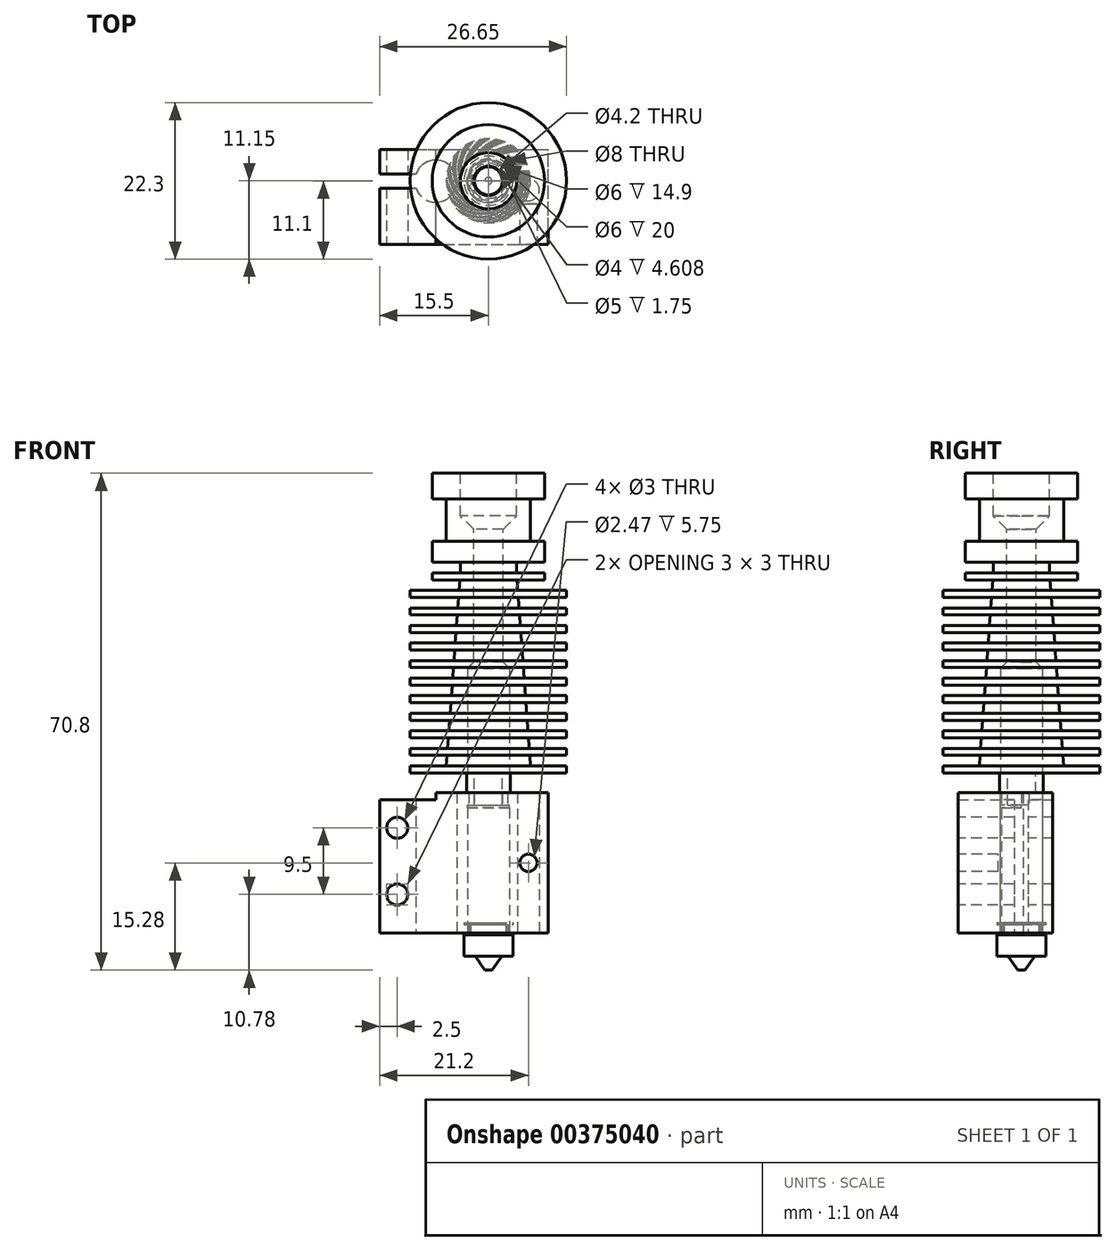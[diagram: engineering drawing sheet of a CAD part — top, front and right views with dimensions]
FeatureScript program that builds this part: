
annotation { "Feature Type Name" : "Feature", "Feature Type Description" : "" }
export const myFeature = defineFeature(function(context is Context, id is Id, definition is map)
    precondition{}
    {
        {
            var Q0;
            Q0=qCreatedBy(makeId("Top.planeOp"),FACE);
            var sketch = newSketch(context, id + "F0", { "sketchPlane" : qUnion([Q0])});
            skCircle(sketch, "E0", {"center": v(0, 0) * mm, "radius": 8 * mm});
            skSolve(sketch);
        }
        {
            var Q0;
            Q0=makeQuery(id+"F0.imprint","IMPRINT",FACE,{"disambiguationData":[TD([[makeQuery(id+"F0.imprint","IMPRINT",EDGE,{"derivedFrom":sQuery(id+"F0.wireOp",EDGE,"E0")}),1.0]])]});
            var Q1;
            Q1=sQuery(id+"F0.wireOp",EDGE,"E0");
            extrude(context, id + "F1", {"entities" : qUnion([Q0]), "surfaceEntities" : qUnion([Q1]), "oppositeDirection" : true, "depth" : 3.7 * mm});
        }
        {
            var Q0;
            Q0=makeQuery(id+"F1.opExtrude","CAP_FACE",FACE,{"disambiguationData":[OSD([sQuery(id+"F0.wireOp",EDGE,"E0")])],"isStart":false});
            var sketch = newSketch(context, id + "F2", { "sketchPlane" : qUnion([Q0])});
            skCircle(sketch, "E1", {"center": v(0, 0) * mm, "radius": 6 * mm});
            skSolve(sketch);
        }
        {
            var Q0;
            Q0=makeQuery(id+"F2.imprint","IMPRINT",FACE,{"disambiguationData":[TD([[makeQuery(id+"F2.imprint","IMPRINT",EDGE,{"derivedFrom":sQuery(id+"F2.wireOp",EDGE,"E1")}),1.0]])]});
            var Q1;
            Q1=sQuery(id+"F2.wireOp",EDGE,"E1");
            extrude(context, id + "F3", {"entities" : qUnion([Q0]), "operationType" : NewBodyOperationType.ADD, "surfaceEntities" : qUnion([Q1]), "depth" : 6 * mm});
        }
        {
            var Q0;
            Q0=makeQuery(id+"F3.opExtrude","CAP_FACE",FACE,{"disambiguationData":[OSD([sQuery(id+"F2.wireOp",EDGE,"E1")])],"isStart":false});
            var sketch = newSketch(context, id + "F4", { "sketchPlane" : qUnion([Q0])});
            skCircle(sketch, "E2", {"center": v(0, 0) * mm, "radius": 8 * mm});
            skSolve(sketch);
        }
        {
            var Q0;
            Q0=qSketchRegion(id+"F4",true);
            extrude(context, id + "F5", {"entities" : qUnion([Q0]), "operationType" : NewBodyOperationType.ADD, "depth" : 3 * mm});
        }
        {
            var Q0;
            Q0=qCreatedBy(makeId("Front.planeOp"),FACE);
            var sketch = newSketch(context, id + "F6", { "sketchPlane" : qUnion([Q0])});
            skLineSegment(sketch, "E3", {"start": v(0, 0) * mm, "end": v(0, -12.7) * mm});
            skLineSegment(sketch, "E4.bottom", {"start": v(0, -12.7) * mm, "end": v(4, -12.7) * mm});
            skLineSegment(sketch, "E4.top", {"start": v(0, -14.2) * mm, "end": v(4, -14.2) * mm});
            skLineSegment(sketch, "E4.left", {"start": v(0, -12.7) * mm, "end": v(0, -14.2) * mm});
            skLineSegment(sketch, "E4.right", {"start": v(4, -12.7) * mm, "end": v(4, -14.2) * mm});
            skLineSegment(sketch, "E5.bottom", {"start": v(0, -14.2) * mm, "end": v(8, -14.2) * mm});
            skLineSegment(sketch, "E5.top", {"start": v(0, -15.2) * mm, "end": v(8, -15.2) * mm});
            skLineSegment(sketch, "E5.left", {"start": v(0, -14.2) * mm, "end": v(0, -15.2) * mm});
            skLineSegment(sketch, "E5.right", {"start": v(8, -14.2) * mm, "end": v(8, -15.2) * mm});
            skLineSegment(sketch, "E6", {"start": v(0, -15.2) * mm, "end": v(0, -16.7) * mm});
            skLineSegment(sketch, "E7.bottom", {"start": v(0, -16.7) * mm, "end": v(11.15, -16.7) * mm});
            skLineSegment(sketch, "E7.top", {"start": v(0, -17.7) * mm, "end": v(11.15, -17.7) * mm});
            skLineSegment(sketch, "E7.left", {"start": v(0, -16.7) * mm, "end": v(0, -17.7) * mm});
            skLineSegment(sketch, "E7.right", {"start": v(11.15, -16.7) * mm, "end": v(11.15, -17.7) * mm});
            skLineSegment(sketch, "E8.1.0.0", {"start": v(0, -20.2) * mm, "end": v(11.15, -20.2) * mm});
            skLineSegment(sketch, "E8.1.0.1", {"start": v(0, -19.2) * mm, "end": v(11.15, -19.2) * mm});
            skLineSegment(sketch, "E8.1.0.2", {"start": v(0, -19.2) * mm, "end": v(0, -20.2) * mm});
            skLineSegment(sketch, "E8.1.0.3", {"start": v(11.15, -19.2) * mm, "end": v(11.15, -20.2) * mm});
            skLineSegment(sketch, "E8.2.0.0", {"start": v(0, -22.7) * mm, "end": v(11.15, -22.7) * mm});
            skLineSegment(sketch, "E8.2.0.1", {"start": v(0, -21.7) * mm, "end": v(11.15, -21.7) * mm});
            skLineSegment(sketch, "E8.2.0.2", {"start": v(0, -21.7) * mm, "end": v(0, -22.7) * mm});
            skLineSegment(sketch, "E8.2.0.3", {"start": v(11.15, -21.7) * mm, "end": v(11.15, -22.7) * mm});
            skLineSegment(sketch, "E8.3.0.0", {"start": v(0, -25.2) * mm, "end": v(11.15, -25.2) * mm});
            skLineSegment(sketch, "E8.3.0.1", {"start": v(0, -24.2) * mm, "end": v(11.15, -24.2) * mm});
            skLineSegment(sketch, "E8.3.0.2", {"start": v(0, -24.2) * mm, "end": v(0, -25.2) * mm});
            skLineSegment(sketch, "E8.3.0.3", {"start": v(11.15, -24.2) * mm, "end": v(11.15, -25.2) * mm});
            skLineSegment(sketch, "E8.4.0.0", {"start": v(0, -27.7) * mm, "end": v(11.15, -27.7) * mm});
            skLineSegment(sketch, "E8.4.0.1", {"start": v(0, -26.7) * mm, "end": v(11.15, -26.7) * mm});
            skLineSegment(sketch, "E8.4.0.2", {"start": v(0, -26.7) * mm, "end": v(0, -27.7) * mm});
            skLineSegment(sketch, "E8.4.0.3", {"start": v(11.15, -26.7) * mm, "end": v(11.15, -27.7) * mm});
            skLineSegment(sketch, "E8.5.0.0", {"start": v(0, -30.2) * mm, "end": v(11.15, -30.2) * mm});
            skLineSegment(sketch, "E8.5.0.1", {"start": v(0, -29.2) * mm, "end": v(11.15, -29.2) * mm});
            skLineSegment(sketch, "E8.5.0.2", {"start": v(0, -29.2) * mm, "end": v(0, -30.2) * mm});
            skLineSegment(sketch, "E8.5.0.3", {"start": v(11.15, -29.2) * mm, "end": v(11.15, -30.2) * mm});
            skLineSegment(sketch, "E8.6.0.0", {"start": v(0, -32.7) * mm, "end": v(11.15, -32.7) * mm});
            skLineSegment(sketch, "E8.6.0.1", {"start": v(0, -31.7) * mm, "end": v(11.15, -31.7) * mm});
            skLineSegment(sketch, "E8.6.0.2", {"start": v(0, -31.7) * mm, "end": v(0, -32.7) * mm});
            skLineSegment(sketch, "E8.6.0.3", {"start": v(11.15, -31.7) * mm, "end": v(11.15, -32.7) * mm});
            skLineSegment(sketch, "E8.7.0.0", {"start": v(0, -35.2) * mm, "end": v(11.15, -35.2) * mm});
            skLineSegment(sketch, "E8.7.0.1", {"start": v(0, -34.2) * mm, "end": v(11.15, -34.2) * mm});
            skLineSegment(sketch, "E8.7.0.2", {"start": v(0, -34.2) * mm, "end": v(0, -35.2) * mm});
            skLineSegment(sketch, "E8.7.0.3", {"start": v(11.15, -34.2) * mm, "end": v(11.15, -35.2) * mm});
            skLineSegment(sketch, "E8.8.0.0", {"start": v(0, -37.7) * mm, "end": v(11.15, -37.7) * mm});
            skLineSegment(sketch, "E8.8.0.1", {"start": v(0, -36.7) * mm, "end": v(11.15, -36.7) * mm});
            skLineSegment(sketch, "E8.8.0.2", {"start": v(0, -36.7) * mm, "end": v(0, -37.7) * mm});
            skLineSegment(sketch, "E8.8.0.3", {"start": v(11.15, -36.7) * mm, "end": v(11.15, -37.7) * mm});
            skLineSegment(sketch, "E8.9.0.0", {"start": v(0, -40.2) * mm, "end": v(11.15, -40.2) * mm});
            skLineSegment(sketch, "E8.9.0.1", {"start": v(0, -39.2) * mm, "end": v(11.15, -39.2) * mm});
            skLineSegment(sketch, "E8.9.0.2", {"start": v(0, -39.2) * mm, "end": v(0, -40.2) * mm});
            skLineSegment(sketch, "E8.9.0.3", {"start": v(11.15, -39.2) * mm, "end": v(11.15, -40.2) * mm});
            skLineSegment(sketch, "E8.10.0.0", {"start": v(0, -42.7) * mm, "end": v(11.15, -42.7) * mm});
            skLineSegment(sketch, "E8.10.0.1", {"start": v(0, -41.7) * mm, "end": v(11.15, -41.7) * mm});
            skLineSegment(sketch, "E8.10.0.2", {"start": v(0, -41.7) * mm, "end": v(0, -42.7) * mm});
            skLineSegment(sketch, "E8.10.0.3", {"start": v(11.15, -41.7) * mm, "end": v(11.15, -42.7) * mm});
            skLineSegment(sketch, "E8.direction1", {"start": v(0, -17.7) * mm, "end": v(0, -20.2) * mm, "construction": true});
            skLineSegment(sketch, "E9", {"start": v(0, -41.7) * mm, "end": v(6, -41.7) * mm});
            skLineSegment(sketch, "E10", {"start": v(4.07, -15.2) * mm, "end": v(4.18, -16.7) * mm});
            skLineSegment(sketch, "E11.trimOffspring", {"start": v(4.25, -17.7) * mm, "end": v(4.36, -19.2) * mm});
            skLineSegment(sketch, "E12.trimOffspring", {"start": v(4.44, -20.2) * mm, "end": v(4.55, -21.7) * mm});
            skLineSegment(sketch, "E13.trimOffspring", {"start": v(4.62, -22.7) * mm, "end": v(4.73, -24.2) * mm});
            skLineSegment(sketch, "E14.trimOffspring", {"start": v(4.8, -25.2) * mm, "end": v(4.9, -26.7) * mm});
            skLineSegment(sketch, "E15.trimOffspring", {"start": v(4.98, -27.7) * mm, "end": v(5.1, -29.2) * mm});
            skLineSegment(sketch, "E16.trimOffspring", {"start": v(5.16, -30.2) * mm, "end": v(5.27, -31.7) * mm});
            skLineSegment(sketch, "E17.trimOffspring", {"start": v(5.35, -32.7) * mm, "end": v(5.45, -34.2) * mm});
            skLineSegment(sketch, "E18.trimOffspring", {"start": v(5.53, -35.2) * mm, "end": v(5.64, -36.7) * mm});
            skLineSegment(sketch, "E19.trimOffspring", {"start": v(5.7, -37.7) * mm, "end": v(5.82, -39.2) * mm});
            skLineSegment(sketch, "E20.trimOffspring", {"start": v(5.9, -40.2) * mm, "end": v(6, -41.7) * mm});
            skLineSegment(sketch, "E21", {"start": v(0, -17.7) * mm, "end": v(0, -19.2) * mm});
            skLineSegment(sketch, "E22", {"start": v(0, -20.2) * mm, "end": v(0, -21.7) * mm});
            skLineSegment(sketch, "E23", {"start": v(0, -22.7) * mm, "end": v(0, -24.2) * mm});
            skLineSegment(sketch, "E24", {"start": v(0, -25.2) * mm, "end": v(0, -26.7) * mm});
            skLineSegment(sketch, "E25", {"start": v(0, -27.7) * mm, "end": v(0, -29.2) * mm});
            skLineSegment(sketch, "E26", {"start": v(0, -30.2) * mm, "end": v(0, -31.7) * mm});
            skLineSegment(sketch, "E27", {"start": v(0, -32.7) * mm, "end": v(0, -34.2) * mm});
            skLineSegment(sketch, "E28", {"start": v(0, -35.2) * mm, "end": v(0, -36.7) * mm});
            skLineSegment(sketch, "E29", {"start": v(0, -37.7) * mm, "end": v(0, -39.2) * mm});
            skLineSegment(sketch, "E30", {"start": v(0, -40.2) * mm, "end": v(0, -41.7) * mm});
            skLineSegment(sketch, "E31.right", {"start": v(3, -42.7) * mm, "end": v(3, -45.2) * mm});
            skLineSegment(sketch, "E32", {"start": v(3, -45.2) * mm, "end": v(2, -45.2) * mm});
            skLineSegment(sketch, "E33", {"start": v(2, -45.2) * mm, "end": v(2, -42.7) * mm});
            skLineSegment(sketch, "E34.bottom", {"start": v(2, -45.2) * mm, "end": v(3, -45.2) * mm});
            skLineSegment(sketch, "E34.top", {"start": v(2, -47.3) * mm, "end": v(3, -47.3) * mm});
            skLineSegment(sketch, "E34.left", {"start": v(2, -45.2) * mm, "end": v(2, -47.3) * mm});
            skLineSegment(sketch, "E34.right", {"start": v(3, -45.2) * mm, "end": v(3, -47.3) * mm});
            skLineSegment(sketch, "E35.bottom", {"start": v(3, -47.3) * mm, "end": v(3.75, -47.3) * mm});
            skLineSegment(sketch, "E35.top", {"start": v(3, -46.56) * mm, "end": v(3.75, -46.56) * mm});
            skLineSegment(sketch, "E35.left", {"start": v(3, -47.3) * mm, "end": v(3, -46.56) * mm});
            skLineSegment(sketch, "E35.right", {"start": v(3.75, -47.3) * mm, "end": v(3.75, -46.56) * mm});
            skLineSegment(sketch, "E36.bottom", {"start": v(2, -42.7) * mm, "end": v(3, -42.7) * mm});
            skLineSegment(sketch, "E36.top", {"start": v(2, -41.7) * mm, "end": v(3, -41.7) * mm});
            skLineSegment(sketch, "E36.left", {"start": v(2, -42.7) * mm, "end": v(2, -41.7) * mm});
            skLineSegment(sketch, "E36.right", {"start": v(3, -42.7) * mm, "end": v(3, -41.7) * mm});
            skSolve(sketch);
        }
        {
            var Q0;
            Q0=qSketchRegion(id+"F6",true);
            var Q1;
            {var subQ0=sQuery(id+"F6.wireOp",EDGE,"E31.right");Q1=makeQuery(id+"F6.imprint","IMPRINT",FACE,{"disambiguationData":[TD([[makeQuery(id+"F6.imprint","IMPRINT",EDGE,{"derivedFrom":subQ0}),-1.0]])]});}
            var Q2;
            Q2=makeQuery(id+"F6.imprint","IMPRINT",FACE,{"disambiguationData":[TD([[makeQuery(id+"F6.imprint","IMPRINT",EDGE,{"derivedFrom":sQuery(id+"F6.wireOp",EDGE,"E34.bottom")}),-1.0]])]});
            var Q3;
            Q3=makeQuery(id+"F6.imprint","IMPRINT",FACE,{"disambiguationData":[TD([[makeQuery(id+"F6.imprint","IMPRINT",EDGE,{"derivedFrom":sQuery(id+"F6.wireOp",EDGE,"E36.bottom")}),1.0]])]});
            var Q4;
            Q4=makeQuery(id+"F6.imprint","IMPRINT",FACE,{"disambiguationData":[TD([[makeQuery(id+"F6.imprint","IMPRINT",EDGE,{"derivedFrom":sQuery(id+"F6.wireOp",EDGE,"E31.right")}),-1.0]])]});
            var Q5;
            Q5=makeQuery(id+"F6.imprint","IMPRINT",FACE,{"disambiguationData":[TD([[makeQuery(id+"F6.imprint","IMPRINT",EDGE,{"derivedFrom":sQuery(id+"F6.wireOp",EDGE,"E34.bottom")}),-1.0]])]});
            var Q6;
            Q6=sQuery(id+"F6.wireOp",EDGE,"E3");
            revolve(context, id + "F7", {"operationType" : NewBodyOperationType.ADD, "entities" : qUnion([Q0, Q1, Q2, Q3, Q4, Q5]), "axis" : qUnion([Q6]), "revolveType" : RevolveType.FULL});
        }
        {
            var Q0;
            Q0=makeQuery(id+"F1.opExtrude","CAP_FACE",FACE,{"disambiguationData":[OSD([sQuery(id+"F0.wireOp",EDGE,"E0")])],"isStart":true});
            var sketch = newSketch(context, id + "F8", { "sketchPlane" : qUnion([Q0])});
            skCircle(sketch, "E37", {"center": v(0, 0) * mm, "radius": 2.1 * mm});
            skSolve(sketch);
        }
        {
            var Q0;
            Q0=qSketchRegion(id+"F8",true);
            extrude(context, id + "F9", {"entities" : qUnion([Q0]), "operationType" : NewBodyOperationType.REMOVE, "oppositeDirection" : true, "depth" : 42.7 * mm});
        }
        {
            var Q0;
            Q0=makeQuery(id+"F1.opExtrude","CAP_FACE",FACE,{"disambiguationData":[OSD([sQuery(id+"F0.wireOp",EDGE,"E0")])],"isStart":true});
            var sketch = newSketch(context, id + "F10", { "sketchPlane" : qUnion([Q0])});
            skCircle(sketch, "E38", {"center": v(0, 0) * mm, "radius": 4 * mm});
            skSolve(sketch);
        }
        {
            var Q0;
            Q0=qSketchRegion(id+"F10",true);
            extrude(context, id + "F11", {"entities" : qUnion([Q0]), "operationType" : NewBodyOperationType.REMOVE, "oppositeDirection" : true, "depth" : 6 * mm});
        }
        {
            var Q0;
            Q0=makeQuery(id+"F11.boolean.opBoolean","INTERSECT",EDGE,{"derivedFrom":[makeQuery(id+"F9.boolean.opBoolean","COPY",FACE,{"derivedFrom":makeQuery(id+"F9.opExtrude","SWEPT_FACE",FACE,{"disambiguationData":[OSD([sQuery(id+"F8.wireOp",EDGE,"E37")])]})}),makeQuery(id+"F11.opExtrude","CAP_FACE",FACE,{"disambiguationData":[OSD([sQuery(id+"F10.wireOp",EDGE,"E38")])],"isStart":false})]});
            chamfer(context, id + "F12", {"entities" : qUnion([Q0]), "width" : 2 * mm, "tangentPropagation" : true});
        }
        {
            var Q0;
            Q0=makeQuery(id+"F7.opRevolve","SWEPT_FACE",FACE,{"disambiguationData":[OSD([sQuery(id+"F6.wireOp",EDGE,"E8.10.0.0")])]});
            var sketch = newSketch(context, id + "F13", { "sketchPlane" : qUnion([Q0])});
            skCircle(sketch, "E39", {"center": v(0, 0) * mm, "radius": 3 * mm});
            skSolve(sketch);
        }
        {
            var Q0;
            Q0=qSketchRegion(id+"F13",true);
            extrude(context, id + "F14", {"entities" : qUnion([Q0]), "operationType" : NewBodyOperationType.REMOVE, "oppositeDirection" : true, "depth" : 14.8 * mm});
        }
        {
            var Q0;
            Q0=makeQuery(id+"F14.boolean.opBoolean","INTERSECT",EDGE,{"derivedFrom":[makeQuery(id+"F9.boolean.opBoolean","COPY",FACE,{"derivedFrom":makeQuery(id+"F9.opExtrude","SWEPT_FACE",FACE,{"disambiguationData":[OSD([sQuery(id+"F8.wireOp",EDGE,"E37")])]})}),makeQuery(id+"F14.opExtrude","CAP_FACE",FACE,{"disambiguationData":[OSD([sQuery(id+"F13.wireOp",EDGE,"E39")])],"isStart":false})]});
            chamfer(context, id + "F15", {"entities" : qUnion([Q0]), "width" : 1 * mm, "tangentPropagation" : true});
        }
        {
            var Q0;
            Q0=qCreatedBy(makeId("Front.planeOp"),FACE);
            var sketch = newSketch(context, id + "F16", { "sketchPlane" : qUnion([Q0])});
            skLineSegment(sketch, "E40.bottom", {"start": v(-7.5, -45.52) * mm, "end": v(8.5, -45.52) * mm});
            skLineSegment(sketch, "E40.top", {"start": v(-15.5, -65.52) * mm, "end": v(8.5, -65.52) * mm});
            skLineSegment(sketch, "E40.right", {"start": v(8.5, -45.52) * mm, "end": v(8.5, -65.52) * mm});
            skLineSegment(sketch, "E41", {"start": v(-15.5, -46.52) * mm, "end": v(-15.5, -65.52) * mm});
            skLineSegment(sketch, "E42", {"start": v(-7.5, -45.52) * mm, "end": v(-7.5, -46.52) * mm});
            skLineSegment(sketch, "E43", {"start": v(-15.5, -46.52) * mm, "end": v(-7.5, -46.52) * mm});
            skSolve(sketch);
        }
        {
            var Q0;
            Q0=makeQuery(id+"F16.imprint","IMPRINT",FACE,{"disambiguationData":[TD([[makeQuery(id+"F16.imprint","IMPRINT",EDGE,{"derivedFrom":sQuery(id+"F16.wireOp",EDGE,"E40.bottom")}),-1.0]])]});
            var Q1;
            Q1=makeQuery(id+"F16.imprint","IMPRINT",FACE,{"disambiguationData":[TD([[makeQuery(id+"F16.imprint","IMPRINT",EDGE,{"derivedFrom":sQuery(id+"F16.wireOp",EDGE,"hSTLO5rz-Z077-ZaO5-nEVS-phWlFBx8dYmu")}),1.0]])]});
            var Q2;
            Q2=makeQuery(id+"F16.imprint","IMPRINT",FACE,{"disambiguationData":[TD([[makeQuery(id+"F16.imprint","IMPRINT",EDGE,{"derivedFrom":sQuery(id+"F16.wireOp",EDGE,"1ucrc5hz-Jwvr-DOmE-K7qY-mdj6J8iSEPF0")}),1.0]])]});
            extrude(context, id + "F17", {"entities" : qUnion([Q0, Q1, Q2]), "endBound" : BoundingType.SYMMETRIC, "depth" : 13.5 * mm});
        }
        {
            var Q0;
            Q0=makeQuery(id+"F17.opExtrude","SWEPT_FACE",FACE,{"disambiguationData":[OSD([sQuery(id+"F16.wireOp",EDGE,"E40.top")])]});
            var sketch = newSketch(context, id + "F18", { "sketchPlane" : qUnion([Q0])});
            skCircle(sketch, "E44", {"center": v(0, -2.25) * mm, "radius": 3 * mm});
            skCircle(sketch, "E45", {"center": v(5.7, -1) * mm, "radius": 1.55 * mm});
            skArc(sketch, "E46", {"start": v(-10.33, -3.25) * mm, "mid": v(-4.5, -2.25) * mm, "end": v(-10.33, -1.25) * mm});
            skLineSegment(sketch, "E47.bottom", {"start": v(-15.5, -1.25) * mm, "end": v(-10.33, -1.25) * mm});
            skLineSegment(sketch, "E47.top", {"start": v(-15.5, -3.25) * mm, "end": v(-10.33, -3.25) * mm});
            skLineSegment(sketch, "E47.left", {"start": v(-15.5, -1.25) * mm, "end": v(-15.5, -3.25) * mm});
            skSolve(sketch);
        }
        {
            var Q0;
            Q0=qSketchRegion(id+"F18",true);
            extrude(context, id + "F19", {"entities" : qUnion([Q0]), "operationType" : NewBodyOperationType.REMOVE, "oppositeDirection" : true, "depth" : 20 * mm});
        }
        {
            var Q0;
            Q0=makeQuery(id+"F17.opExtrude","SWEPT_BODY",BODY,{"disambiguationData":[OSD([sQuery(id+"F16.wireOp",EDGE,"E40.bottom"),sQuery(id+"F16.wireOp",EDGE,"E40.top"),sQuery(id+"F16.wireOp",EDGE,"E40.right"),sQuery(id+"F16.wireOp",EDGE,"E41"),sQuery(id+"F16.wireOp",EDGE,"E42"),sQuery(id+"F16.wireOp",EDGE,"E43")])]});
            var Q1;
            Q1=qCreatedBy(makeId("Origin.pointOp"),VERTEX);
            var Q2;
            Q2=makeQuery(id+"F19.boolean.opBoolean","COPY",EDGE,{"derivedFrom":makeQuery(id+"F19.opExtrude","CAP_EDGE",EDGE,{"disambiguationData":[OSD([sQuery(id+"F18.wireOp",EDGE,"E44")])],"isStart":true})});
            var Q3;
            Q3=qCreatedBy(makeId("Front.planeOp"),FACE);
            transform(context, id + "F20", {"entities" : qUnion([Q0]), "transformType" : TransformType.TRANSLATION_DISTANCE, "transformDirection" : qUnion([Q3]), "distance" : 2.3 * mm, "makeCopy" : false});
        }
        {
            var Q0;
            Q0=qCreatedBy(makeId("Front.planeOp"),FACE);
            var sketch = newSketch(context, id + "F21", { "sketchPlane" : qUnion([Q0])});
            skLineSegment(sketch, "E48.bottom", {"start": v(0, -65.8) * mm, "end": v(3.5, -65.8) * mm});
            skLineSegment(sketch, "E48.right", {"start": v(3.5, -65.8) * mm, "end": v(3.5, -68.8) * mm});
            skLineSegment(sketch, "E49.top", {"start": v(0, -70.8) * mm, "end": v(0.5, -70.8) * mm});
            skLineSegment(sketch, "E50", {"start": v(0.5, -70.8) * mm, "end": v(1.9, -68.8) * mm});
            skLineSegment(sketch, "E51.trimOffspring", {"start": v(1.9, -68.8) * mm, "end": v(3.5, -68.8) * mm});
            skLineSegment(sketch, "E52", {"start": v(0, -70.8) * mm, "end": v(0, -65.8) * mm});
            skLineSegment(sketch, "E53", {"start": v(0, -65.8) * mm, "end": v(2.5, -65.8) * mm});
            skLineSegment(sketch, "E54", {"start": v(2.5, -65.8) * mm, "end": v(2.5, -64.3) * mm});
            skLineSegment(sketch, "E55", {"start": v(2.5, -64.3) * mm, "end": v(2.75, -64.3) * mm});
            skLineSegment(sketch, "E56", {"start": v(2.75, -64.3) * mm, "end": v(2.75, -65.8) * mm});
            skLineSegment(sketch, "E57.bottom", {"start": v(2.5, -64.3) * mm, "end": v(3.5, -64.3) * mm});
            skLineSegment(sketch, "E57.top", {"start": v(2.5, -64.05) * mm, "end": v(3.5, -64.05) * mm});
            skLineSegment(sketch, "E57.left", {"start": v(2.5, -64.3) * mm, "end": v(2.5, -64.05) * mm});
            skLineSegment(sketch, "E57.right", {"start": v(3.5, -64.3) * mm, "end": v(3.5, -64.05) * mm});
            skSolve(sketch);
        }
        {
            var Q0;
            Q0=qSketchRegion(id+"F21",true);
            var Q1;
            Q1=sQuery(id+"F21.wireOp",EDGE,"E52");
            revolve(context, id + "F22", {"entities" : qUnion([Q0]), "axis" : qUnion([Q1]), "revolveType" : RevolveType.FULL});
        }
        {
            var Q0;
            Q0=makeQuery(id+"F17.opExtrude","CAP_FACE",FACE,{"disambiguationData":[OSD([sQuery(id+"F16.wireOp",EDGE,"E40.bottom"),sQuery(id+"F16.wireOp",EDGE,"E40.top"),sQuery(id+"F16.wireOp",EDGE,"E40.left"),sQuery(id+"F16.wireOp",EDGE,"E40.right"),sQuery(id+"F16.wireOp",EDGE,"UV7SLQof-a04S-M22U-fSmA-h1v0EtluGPG8"),sQuery(id+"F16.wireOp",EDGE,"g7xF2yxM-ANDZ-qpWR-qvBO-6FQJMMhnbeDq.top"),sQuery(id+"F16.wireOp",EDGE,"L5R9zHDy-imt3-tSqA-0CQm-Dj3PFv1zczeX.top"),sQuery(id+"F16.wireOp",EDGE,"56c6f5e6-72b2-44f0-a3dc-ebd65ac1d403.trimOffspring")])],"isStart":false});
            var sketch = newSketch(context, id + "F23", { "sketchPlane" : qUnion([Q0])});
            skCircle(sketch, "E58", {"center": v(-13, -60.02) * mm, "radius": 1.5 * mm});
            skCircle(sketch, "E59", {"center": v(-13, -50.52) * mm, "radius": 1.5 * mm});
            skCircle(sketch, "E60", {"center": v(5.7, -55.52) * mm, "radius": 1.23 * mm});
            skSolve(sketch);
        }
        {
            var Q0;
            Q0=makeQuery(id+"F23.imprint","IMPRINT",FACE,{"disambiguationData":[TD([[makeQuery(id+"F23.imprint","IMPRINT",EDGE,{"derivedFrom":sQuery(id+"F23.wireOp",EDGE,"E60")}),1.0]])]});
            extrude(context, id + "F24", {"entities" : qUnion([Q0]), "operationType" : NewBodyOperationType.REMOVE, "oppositeDirection" : true, "depth" : 5.75 * mm});
        }
        {
            var Q0;
            Q0=makeQuery(id+"F23.imprint","IMPRINT",FACE,{"disambiguationData":[TD([[makeQuery(id+"F23.imprint","IMPRINT",EDGE,{"derivedFrom":sQuery(id+"F23.wireOp",EDGE,"E59")}),1.0]])]});
            var Q1;
            Q1=makeQuery(id+"F23.imprint","IMPRINT",FACE,{"disambiguationData":[TD([[makeQuery(id+"F23.imprint","IMPRINT",EDGE,{"derivedFrom":sQuery(id+"F23.wireOp",EDGE,"E58")}),1.0]])]});
            var Q2;
            Q2=makeQuery(id+"F17.opExtrude","CAP_FACE",FACE,{"disambiguationData":[OSD([sQuery(id+"F16.wireOp",EDGE,"E40.bottom"),sQuery(id+"F16.wireOp",EDGE,"E40.top"),sQuery(id+"F16.wireOp",EDGE,"E40.right"),sQuery(id+"F16.wireOp",EDGE,"E41"),sQuery(id+"F16.wireOp",EDGE,"E42"),sQuery(id+"F16.wireOp",EDGE,"E43")])],"isStart":true});
            extrude(context, id + "F25", {"entities" : qUnion([Q0, Q1]), "operationType" : NewBodyOperationType.REMOVE, "endBound" : BoundingType.UP_TO_SURFACE, "oppositeDirection" : true, "endBoundEntityFace" : qUnion([Q2]), "depth" : 4.5 * mm});
        }
        {
            var Q0;
            {var subQ0=sQuery(id+"F6.wireOp",EDGE,"E8.10.0.0");Q0=makeQuery(id+"F7.opRevolve","SWEPT_FACE",FACE,{"disambiguationData":[OSD([subQ0]),TDD([makeQuery(id+"F6.imprint","IMPRINT",EDGE,{"disambiguationData":[TD([[makeQuery(id+"F6.imprint","INTERSECT",VERTEX,{"derivedFrom":[subQ0,sQuery(id+"F6.wireOp",EDGE,"E8.10.0.3")]}),1.0]])],"derivedFrom":subQ0})])]});}
            var sketch = newSketch(context, id + "F26", { "sketchPlane" : qUnion([Q0])});
            skCircle(sketch, "E61", {"center": v(0, 0) * mm, "radius": 3.12 * mm});
            skSolve(sketch);
        }
        {
            var Q0;
            Q0=makeQuery(id+"F26.imprint","IMPRINT",FACE,{"disambiguationData":[TD([[makeQuery(id+"F26.imprint","IMPRINT",EDGE,{"derivedFrom":sQuery(id+"F26.wireOp",EDGE,"E61")}),1.0]])]});
            extrude(context, id + "F27", {"entities" : qUnion([Q0]), "operationType" : NewBodyOperationType.ADD, "depth" : 5 * mm});
        }
    });
